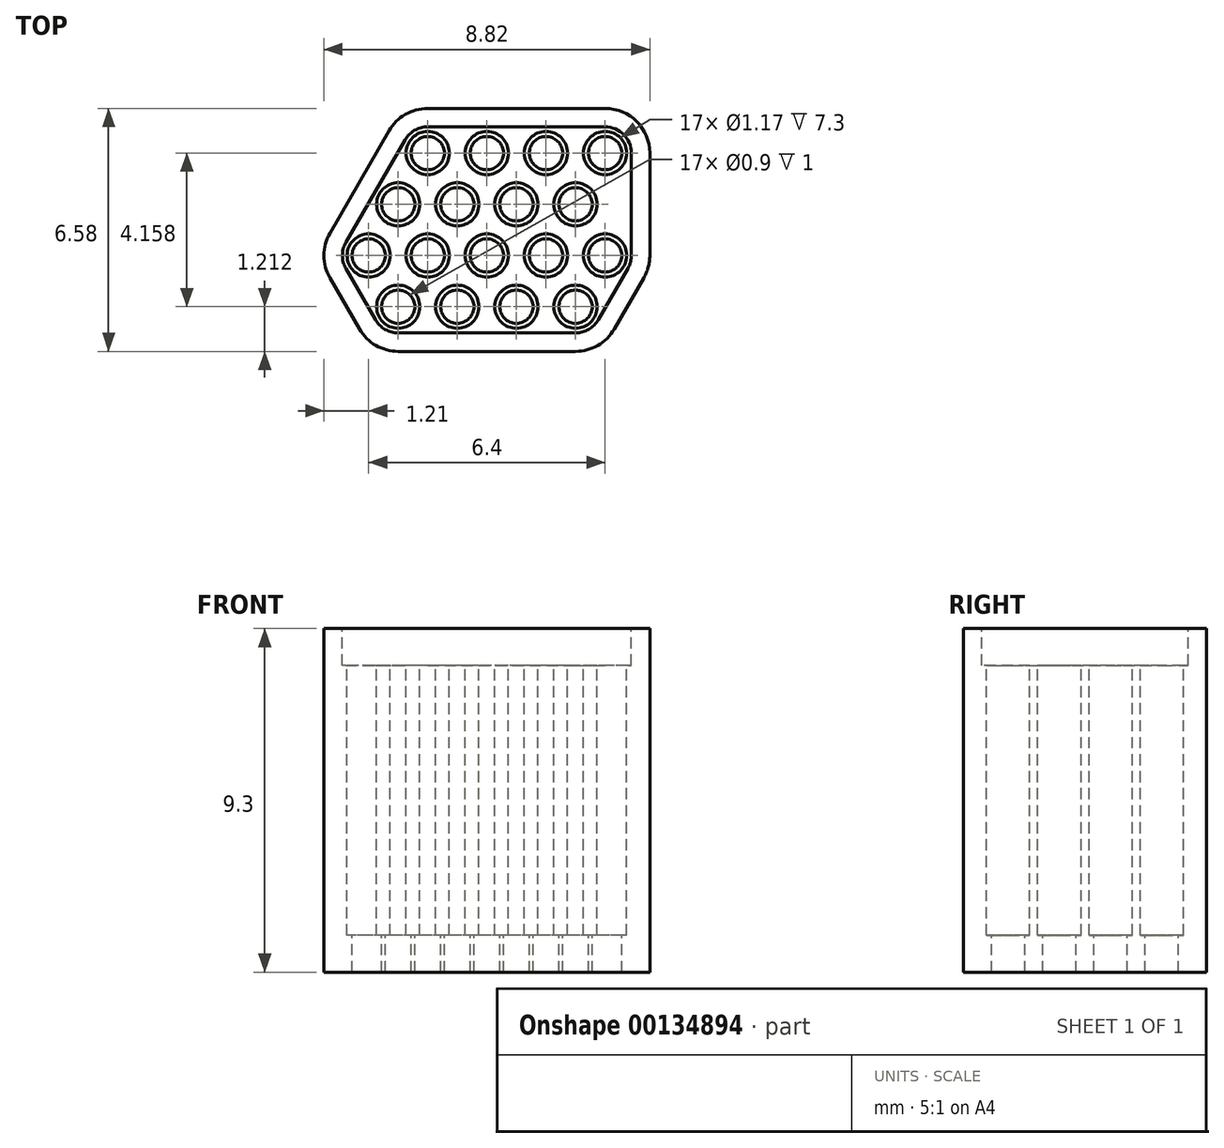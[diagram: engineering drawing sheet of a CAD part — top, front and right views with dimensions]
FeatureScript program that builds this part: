
annotation { "Feature Type Name" : "Feature", "Feature Type Description" : "" }
export const myFeature = defineFeature(function(context is Context, id is Id, definition is map)
    precondition{}
    {
        {
            var Q0;
            Q0=qCreatedBy(makeId("Top.planeOp"),FACE);
            var sketch = newSketch(context, id + "F0", { "sketchPlane" : qUnion([Q0])});
            skLineSegment(sketch, "E0", {"start": v(-0.8, 0) * mm, "end": v(-0.8, -4.16) * mm, "construction": true});
            skCircle(sketch, "E1", {"center": v(0, 0) * mm, "radius": 0.58 * mm});
            skCircle(sketch, "E2", {"center": v(0, -2.77) * mm, "radius": 0.58 * mm});
            skCircle(sketch, "E3", {"center": v(-0.8, -1.39) * mm, "radius": 0.58 * mm});
            skCircle(sketch, "E4", {"center": v(-0.8, -4.16) * mm, "radius": 0.58 * mm});
            skCircle(sketch, "E5.1.0.0", {"center": v(-1.6, 0) * mm, "radius": 0.58 * mm});
            skCircle(sketch, "E5.1.0.1", {"center": v(-2.4, -1.39) * mm, "radius": 0.58 * mm});
            skCircle(sketch, "E5.1.0.2", {"center": v(-2.4, -4.16) * mm, "radius": 0.58 * mm});
            skCircle(sketch, "E5.1.0.3", {"center": v(-1.6, -2.77) * mm, "radius": 0.58 * mm});
            skCircle(sketch, "E5.2.0.0", {"center": v(-3.2, 0) * mm, "radius": 0.58 * mm});
            skCircle(sketch, "E5.2.0.1", {"center": v(-4, -1.39) * mm, "radius": 0.58 * mm});
            skCircle(sketch, "E5.2.0.2", {"center": v(-4, -4.16) * mm, "radius": 0.58 * mm});
            skCircle(sketch, "E5.2.0.3", {"center": v(-3.2, -2.77) * mm, "radius": 0.58 * mm});
            skCircle(sketch, "E5.3.0.0", {"center": v(-4.8, 0) * mm, "radius": 0.58 * mm});
            skCircle(sketch, "E5.3.0.1", {"center": v(-5.6, -1.39) * mm, "radius": 0.58 * mm});
            skCircle(sketch, "E5.3.0.2", {"center": v(-5.6, -4.16) * mm, "radius": 0.58 * mm});
            skCircle(sketch, "E5.3.0.3", {"center": v(-4.8, -2.77) * mm, "radius": 0.58 * mm});
            skLineSegment(sketch, "E5.direction1", {"start": v(-0.8, -4.16) * mm, "end": v(-2.4, -4.16) * mm, "construction": true});
            skCircle(sketch, "E6.1.0.0", {"center": v(-6.4, -2.77) * mm, "radius": 0.58 * mm});
            skLineSegment(sketch, "E6.direction1", {"start": v(-4.8, -2.77) * mm, "end": v(-6.4, -2.77) * mm, "construction": true});
            skLineSegment(sketch, "E7", {"start": v(-6.4, -2.77) * mm, "end": v(-4.8, 0) * mm, "construction": true});
            skLineSegment(sketch, "E8", {"start": v(-4.8, 0) * mm, "end": v(0, 0) * mm, "construction": true});
            skLineSegment(sketch, "E9", {"start": v(0, 0) * mm, "end": v(0, -2.77) * mm, "construction": true});
            skLineSegment(sketch, "E10", {"start": v(0, -2.77) * mm, "end": v(-0.8, -4.16) * mm, "construction": true});
            skLineSegment(sketch, "E11", {"start": v(-5.6, -4.16) * mm, "end": v(-0.8, -4.16) * mm, "construction": true});
            skLineSegment(sketch, "E12", {"start": v(-5.6, -4.16) * mm, "end": v(-6.4, -2.77) * mm, "construction": true});
            skLineSegment(sketch, "E13.0", {"start": v(-6, -4.87) * mm, "end": v(-7.22, -2.77) * mm, "construction": true});
            skLineSegment(sketch, "E13.1", {"start": v(-5.2, 0.7) * mm, "end": v(0.71, 0.71) * mm, "construction": true});
            skLineSegment(sketch, "E13.2", {"start": v(0.71, 0.71) * mm, "end": v(0.71, -2.96) * mm, "construction": true});
            skLineSegment(sketch, "E13.3", {"start": v(-7.22, -2.77) * mm, "end": v(-5.2, 0.71) * mm, "construction": true});
            skLineSegment(sketch, "E13.4", {"start": v(0.71, -2.96) * mm, "end": v(-0.4, -4.87) * mm, "construction": true});
            skLineSegment(sketch, "E13.5", {"start": v(-6, -4.87) * mm, "end": v(-0.4, -4.87) * mm, "construction": true});
            skArc(sketch, "E14", {"start": v(-4.8, 0.7) * mm, "mid": v(-5.16, 0.61) * mm, "end": v(-5.41, 0.35) * mm});
            skArc(sketch, "E15", {"start": v(-7.01, -2.42) * mm, "mid": v(-7.11, -2.77) * mm, "end": v(-7.01, -3.13) * mm});
            skArc(sketch, "E16", {"start": v(-6.21, -4.51) * mm, "mid": v(-5.96, -4.77) * mm, "end": v(-5.6, -4.87) * mm});
            skArc(sketch, "E17", {"start": v(-0.8, -4.87) * mm, "mid": v(-0.44, -4.77) * mm, "end": v(-0.19, -4.51) * mm});
            skArc(sketch, "E18", {"start": v(0.61, -3.13) * mm, "mid": v(0.69, -2.96) * mm, "end": v(0.71, -2.77) * mm});
            skArc(sketch, "E19", {"start": v(0.71, 0) * mm, "mid": v(0.5, 0.5) * mm, "end": v(0, 0.71) * mm});
            skLineSegment(sketch, "E20", {"start": v(-7.01, -2.42) * mm, "end": v(-5.41, 0.35) * mm});
            skLineSegment(sketch, "E21", {"start": v(-4.8, 0.7) * mm, "end": v(0, 0.71) * mm});
            skLineSegment(sketch, "E22", {"start": v(0.71, 0) * mm, "end": v(0.71, -2.77) * mm});
            skLineSegment(sketch, "E23", {"start": v(0.61, -3.13) * mm, "end": v(-0.19, -4.51) * mm});
            skLineSegment(sketch, "E24", {"start": v(-0.8, -4.87) * mm, "end": v(-5.6, -4.87) * mm});
            skLineSegment(sketch, "E25", {"start": v(-6.21, -4.51) * mm, "end": v(-7.01, -3.13) * mm});
            skArc(sketch, "E26.0", {"start": v(-4.8, 1.21) * mm, "mid": v(-5.4, 1.05) * mm, "end": v(-5.85, 0.6) * mm});
            skLineSegment(sketch, "E26.1", {"start": v(1.05, -3.38) * mm, "end": v(0.25, -4.76) * mm});
            skArc(sketch, "E26.2", {"start": v(1.05, -3.38) * mm, "mid": v(1.17, -3.09) * mm, "end": v(1.21, -2.77) * mm});
            skLineSegment(sketch, "E26.3", {"start": v(1.21, 0) * mm, "end": v(1.21, -2.77) * mm});
            skArc(sketch, "E26.4", {"start": v(1.21, 0) * mm, "mid": v(0.86, 0.86) * mm, "end": v(0, 1.21) * mm});
            skArc(sketch, "E26.5", {"start": v(-0.8, -5.37) * mm, "mid": v(-0.2, -5.2) * mm, "end": v(0.25, -4.76) * mm});
            skLineSegment(sketch, "E26.6", {"start": v(-4.8, 1.2) * mm, "end": v(0, 1.21) * mm});
            skLineSegment(sketch, "E26.7", {"start": v(-0.8, -5.37) * mm, "end": v(-5.6, -5.37) * mm});
            skArc(sketch, "E26.8", {"start": v(-6.65, -4.76) * mm, "mid": v(-6.2, -5.2) * mm, "end": v(-5.6, -5.37) * mm});
            skLineSegment(sketch, "E26.9", {"start": v(-6.65, -4.76) * mm, "end": v(-7.45, -3.38) * mm});
            skArc(sketch, "E26.10", {"start": v(-7.45, -2.17) * mm, "mid": v(-7.61, -2.77) * mm, "end": v(-7.45, -3.38) * mm});
            skLineSegment(sketch, "E26.11", {"start": v(-7.45, -2.17) * mm, "end": v(-5.85, 0.6) * mm});
            skSolve(sketch);
        }
        {
            var Q0;
            Q0=makeQuery(id+"F0.imprint","IMPRINT",FACE,{"disambiguationData":[TD([[makeQuery(id+"F0.imprint","IMPRINT",EDGE,{"derivedFrom":sQuery(id+"F0.wireOp",EDGE,"E14")}),-1.0]])]});
            var Q1;
            Q1=makeQuery(id+"F0.imprint","IMPRINT",FACE,{"disambiguationData":[TD([[makeQuery(id+"F0.imprint","IMPRINT",EDGE,{"derivedFrom":sQuery(id+"F0.wireOp",EDGE,"E1")}),-1.0]])]});
            var Q2;
            Q2=makeQuery(id+"F0.imprint","IMPRINT",FACE,{"disambiguationData":[TD([[makeQuery(id+"F0.imprint","IMPRINT",EDGE,{"derivedFrom":sQuery(id+"F0.wireOp",EDGE,"E4")}),1.0]])]});
            var Q3;
            Q3=makeQuery(id+"F0.imprint","IMPRINT",FACE,{"disambiguationData":[TD([[makeQuery(id+"F0.imprint","IMPRINT",EDGE,{"derivedFrom":sQuery(id+"F0.wireOp",EDGE,"E2")}),1.0]])]});
            var Q4;
            Q4=makeQuery(id+"F0.imprint","IMPRINT",FACE,{"disambiguationData":[TD([[makeQuery(id+"F0.imprint","IMPRINT",EDGE,{"derivedFrom":sQuery(id+"F0.wireOp",EDGE,"E3")}),1.0]])]});
            var Q5;
            Q5=makeQuery(id+"F0.imprint","IMPRINT",FACE,{"disambiguationData":[TD([[makeQuery(id+"F0.imprint","IMPRINT",EDGE,{"derivedFrom":sQuery(id+"F0.wireOp",EDGE,"E1")}),1.0]])]});
            var Q6;
            Q6=makeQuery(id+"F0.imprint","IMPRINT",FACE,{"disambiguationData":[TD([[makeQuery(id+"F0.imprint","IMPRINT",EDGE,{"derivedFrom":sQuery(id+"F0.wireOp",EDGE,"E5.1.0.0")}),1.0]])]});
            var Q7;
            Q7=makeQuery(id+"F0.imprint","IMPRINT",FACE,{"disambiguationData":[TD([[makeQuery(id+"F0.imprint","IMPRINT",EDGE,{"derivedFrom":sQuery(id+"F0.wireOp",EDGE,"E5.2.0.0")}),1.0]])]});
            var Q8;
            Q8=makeQuery(id+"F0.imprint","IMPRINT",FACE,{"disambiguationData":[TD([[makeQuery(id+"F0.imprint","IMPRINT",EDGE,{"derivedFrom":sQuery(id+"F0.wireOp",EDGE,"E5.3.0.0")}),1.0]])]});
            var Q9;
            Q9=makeQuery(id+"F0.imprint","IMPRINT",FACE,{"disambiguationData":[TD([[makeQuery(id+"F0.imprint","IMPRINT",EDGE,{"derivedFrom":sQuery(id+"F0.wireOp",EDGE,"E5.3.0.1")}),1.0]])]});
            var Q10;
            Q10=makeQuery(id+"F0.imprint","IMPRINT",FACE,{"disambiguationData":[TD([[makeQuery(id+"F0.imprint","IMPRINT",EDGE,{"derivedFrom":sQuery(id+"F0.wireOp",EDGE,"E5.2.0.1")}),1.0]])]});
            var Q11;
            Q11=makeQuery(id+"F0.imprint","IMPRINT",FACE,{"disambiguationData":[TD([[makeQuery(id+"F0.imprint","IMPRINT",EDGE,{"derivedFrom":sQuery(id+"F0.wireOp",EDGE,"E5.1.0.1")}),1.0]])]});
            var Q12;
            Q12=makeQuery(id+"F0.imprint","IMPRINT",FACE,{"disambiguationData":[TD([[makeQuery(id+"F0.imprint","IMPRINT",EDGE,{"derivedFrom":sQuery(id+"F0.wireOp",EDGE,"E5.1.0.3")}),1.0]])]});
            var Q13;
            Q13=makeQuery(id+"F0.imprint","IMPRINT",FACE,{"disambiguationData":[TD([[makeQuery(id+"F0.imprint","IMPRINT",EDGE,{"derivedFrom":sQuery(id+"F0.wireOp",EDGE,"E5.2.0.3")}),1.0]])]});
            var Q14;
            Q14=makeQuery(id+"F0.imprint","IMPRINT",FACE,{"disambiguationData":[TD([[makeQuery(id+"F0.imprint","IMPRINT",EDGE,{"derivedFrom":sQuery(id+"F0.wireOp",EDGE,"E6.1.0.0")}),1.0]])]});
            var Q15;
            Q15=makeQuery(id+"F0.imprint","IMPRINT",FACE,{"disambiguationData":[TD([[makeQuery(id+"F0.imprint","IMPRINT",EDGE,{"derivedFrom":sQuery(id+"F0.wireOp",EDGE,"E5.3.0.2")}),1.0]])]});
            var Q16;
            Q16=makeQuery(id+"F0.imprint","IMPRINT",FACE,{"disambiguationData":[TD([[makeQuery(id+"F0.imprint","IMPRINT",EDGE,{"derivedFrom":sQuery(id+"F0.wireOp",EDGE,"E5.2.0.2")}),1.0]])]});
            var Q17;
            Q17=makeQuery(id+"F0.imprint","IMPRINT",FACE,{"disambiguationData":[TD([[makeQuery(id+"F0.imprint","IMPRINT",EDGE,{"derivedFrom":sQuery(id+"F0.wireOp",EDGE,"E5.1.0.2")}),1.0]])]});
            var Q18;
            Q18=makeQuery(id+"F0.imprint","IMPRINT",FACE,{"disambiguationData":[TD([[makeQuery(id+"F0.imprint","IMPRINT",EDGE,{"derivedFrom":sQuery(id+"F0.wireOp",EDGE,"E5.3.0.3")}),1.0]])]});
            extrude(context, id + "F1", {"entities" : qUnion([Q0, Q1, Q2, Q3, Q4, Q5, Q6, Q7, Q8, Q9, Q10, Q11, Q12, Q13, Q14, Q15, Q16, Q17, Q18]), "oppositeDirection" : true, "depth" : 9.3 * mm});
        }
        {
            var Q0;
            Q0=makeQuery(id+"F0.imprint","IMPRINT",FACE,{"disambiguationData":[TD([[makeQuery(id+"F0.imprint","IMPRINT",EDGE,{"derivedFrom":sQuery(id+"F0.wireOp",EDGE,"E1")}),-1.0]])]});
            var Q1;
            Q1=makeQuery(id+"F0.imprint","IMPRINT",FACE,{"disambiguationData":[TD([[makeQuery(id+"F0.imprint","IMPRINT",EDGE,{"derivedFrom":sQuery(id+"F0.wireOp",EDGE,"E5.3.0.0")}),1.0]])]});
            var Q2;
            Q2=makeQuery(id+"F0.imprint","IMPRINT",FACE,{"disambiguationData":[TD([[makeQuery(id+"F0.imprint","IMPRINT",EDGE,{"derivedFrom":sQuery(id+"F0.wireOp",EDGE,"E5.3.0.1")}),1.0]])]});
            var Q3;
            Q3=makeQuery(id+"F0.imprint","IMPRINT",FACE,{"disambiguationData":[TD([[makeQuery(id+"F0.imprint","IMPRINT",EDGE,{"derivedFrom":sQuery(id+"F0.wireOp",EDGE,"E6.1.0.0")}),1.0]])]});
            var Q4;
            Q4=makeQuery(id+"F0.imprint","IMPRINT",FACE,{"disambiguationData":[TD([[makeQuery(id+"F0.imprint","IMPRINT",EDGE,{"derivedFrom":sQuery(id+"F0.wireOp",EDGE,"E5.3.0.2")}),1.0]])]});
            var Q5;
            Q5=makeQuery(id+"F0.imprint","IMPRINT",FACE,{"disambiguationData":[TD([[makeQuery(id+"F0.imprint","IMPRINT",EDGE,{"derivedFrom":sQuery(id+"F0.wireOp",EDGE,"E5.3.0.3")}),1.0]])]});
            var Q6;
            Q6=makeQuery(id+"F0.imprint","IMPRINT",FACE,{"disambiguationData":[TD([[makeQuery(id+"F0.imprint","IMPRINT",EDGE,{"derivedFrom":sQuery(id+"F0.wireOp",EDGE,"E5.2.0.2")}),1.0]])]});
            var Q7;
            Q7=makeQuery(id+"F0.imprint","IMPRINT",FACE,{"disambiguationData":[TD([[makeQuery(id+"F0.imprint","IMPRINT",EDGE,{"derivedFrom":sQuery(id+"F0.wireOp",EDGE,"E5.2.0.1")}),1.0]])]});
            var Q8;
            Q8=makeQuery(id+"F0.imprint","IMPRINT",FACE,{"disambiguationData":[TD([[makeQuery(id+"F0.imprint","IMPRINT",EDGE,{"derivedFrom":sQuery(id+"F0.wireOp",EDGE,"E5.2.0.0")}),1.0]])]});
            var Q9;
            Q9=makeQuery(id+"F0.imprint","IMPRINT",FACE,{"disambiguationData":[TD([[makeQuery(id+"F0.imprint","IMPRINT",EDGE,{"derivedFrom":sQuery(id+"F0.wireOp",EDGE,"E5.1.0.0")}),1.0]])]});
            var Q10;
            Q10=makeQuery(id+"F0.imprint","IMPRINT",FACE,{"disambiguationData":[TD([[makeQuery(id+"F0.imprint","IMPRINT",EDGE,{"derivedFrom":sQuery(id+"F0.wireOp",EDGE,"E5.1.0.1")}),1.0]])]});
            var Q11;
            Q11=makeQuery(id+"F0.imprint","IMPRINT",FACE,{"disambiguationData":[TD([[makeQuery(id+"F0.imprint","IMPRINT",EDGE,{"derivedFrom":sQuery(id+"F0.wireOp",EDGE,"E5.2.0.3")}),1.0]])]});
            var Q12;
            Q12=makeQuery(id+"F0.imprint","IMPRINT",FACE,{"disambiguationData":[TD([[makeQuery(id+"F0.imprint","IMPRINT",EDGE,{"derivedFrom":sQuery(id+"F0.wireOp",EDGE,"E5.1.0.2")}),1.0]])]});
            var Q13;
            Q13=makeQuery(id+"F0.imprint","IMPRINT",FACE,{"disambiguationData":[TD([[makeQuery(id+"F0.imprint","IMPRINT",EDGE,{"derivedFrom":sQuery(id+"F0.wireOp",EDGE,"E1")}),1.0]])]});
            var Q14;
            Q14=makeQuery(id+"F0.imprint","IMPRINT",FACE,{"disambiguationData":[TD([[makeQuery(id+"F0.imprint","IMPRINT",EDGE,{"derivedFrom":sQuery(id+"F0.wireOp",EDGE,"E3")}),1.0]])]});
            var Q15;
            Q15=makeQuery(id+"F0.imprint","IMPRINT",FACE,{"disambiguationData":[TD([[makeQuery(id+"F0.imprint","IMPRINT",EDGE,{"derivedFrom":sQuery(id+"F0.wireOp",EDGE,"E5.1.0.3")}),1.0]])]});
            var Q16;
            Q16=makeQuery(id+"F0.imprint","IMPRINT",FACE,{"disambiguationData":[TD([[makeQuery(id+"F0.imprint","IMPRINT",EDGE,{"derivedFrom":sQuery(id+"F0.wireOp",EDGE,"E4")}),1.0]])]});
            var Q17;
            Q17=makeQuery(id+"F0.imprint","IMPRINT",FACE,{"disambiguationData":[TD([[makeQuery(id+"F0.imprint","IMPRINT",EDGE,{"derivedFrom":sQuery(id+"F0.wireOp",EDGE,"E2")}),1.0]])]});
            extrude(context, id + "F2", {"entities" : qUnion([Q0, Q1, Q2, Q3, Q4, Q5, Q6, Q7, Q8, Q9, Q10, Q11, Q12, Q13, Q14, Q15, Q16, Q17]), "operationType" : NewBodyOperationType.REMOVE, "oppositeDirection" : true, "depth" : 1 * mm});
        }
        {
            var Q0;
            Q0=makeQuery(id+"F0.imprint","IMPRINT",FACE,{"disambiguationData":[TD([[makeQuery(id+"F0.imprint","IMPRINT",EDGE,{"derivedFrom":sQuery(id+"F0.wireOp",EDGE,"E6.1.0.0")}),1.0]])]});
            var Q1;
            Q1=makeQuery(id+"F0.imprint","IMPRINT",FACE,{"disambiguationData":[TD([[makeQuery(id+"F0.imprint","IMPRINT",EDGE,{"derivedFrom":sQuery(id+"F0.wireOp",EDGE,"E5.3.0.1")}),1.0]])]});
            var Q2;
            Q2=makeQuery(id+"F0.imprint","IMPRINT",FACE,{"disambiguationData":[TD([[makeQuery(id+"F0.imprint","IMPRINT",EDGE,{"derivedFrom":sQuery(id+"F0.wireOp",EDGE,"E5.3.0.0")}),1.0]])]});
            var Q3;
            Q3=makeQuery(id+"F0.imprint","IMPRINT",FACE,{"disambiguationData":[TD([[makeQuery(id+"F0.imprint","IMPRINT",EDGE,{"derivedFrom":sQuery(id+"F0.wireOp",EDGE,"E5.3.0.2")}),1.0]])]});
            var Q4;
            Q4=makeQuery(id+"F0.imprint","IMPRINT",FACE,{"disambiguationData":[TD([[makeQuery(id+"F0.imprint","IMPRINT",EDGE,{"derivedFrom":sQuery(id+"F0.wireOp",EDGE,"E5.3.0.3")}),1.0]])]});
            var Q5;
            Q5=makeQuery(id+"F0.imprint","IMPRINT",FACE,{"disambiguationData":[TD([[makeQuery(id+"F0.imprint","IMPRINT",EDGE,{"derivedFrom":sQuery(id+"F0.wireOp",EDGE,"E5.2.0.1")}),1.0]])]});
            var Q6;
            Q6=makeQuery(id+"F0.imprint","IMPRINT",FACE,{"disambiguationData":[TD([[makeQuery(id+"F0.imprint","IMPRINT",EDGE,{"derivedFrom":sQuery(id+"F0.wireOp",EDGE,"E5.2.0.0")}),1.0]])]});
            var Q7;
            Q7=makeQuery(id+"F0.imprint","IMPRINT",FACE,{"disambiguationData":[TD([[makeQuery(id+"F0.imprint","IMPRINT",EDGE,{"derivedFrom":sQuery(id+"F0.wireOp",EDGE,"E5.1.0.0")}),1.0]])]});
            var Q8;
            Q8=makeQuery(id+"F0.imprint","IMPRINT",FACE,{"disambiguationData":[TD([[makeQuery(id+"F0.imprint","IMPRINT",EDGE,{"derivedFrom":sQuery(id+"F0.wireOp",EDGE,"E5.1.0.1")}),1.0]])]});
            var Q9;
            Q9=makeQuery(id+"F0.imprint","IMPRINT",FACE,{"disambiguationData":[TD([[makeQuery(id+"F0.imprint","IMPRINT",EDGE,{"derivedFrom":sQuery(id+"F0.wireOp",EDGE,"E5.2.0.3")}),1.0]])]});
            var Q10;
            Q10=makeQuery(id+"F0.imprint","IMPRINT",FACE,{"disambiguationData":[TD([[makeQuery(id+"F0.imprint","IMPRINT",EDGE,{"derivedFrom":sQuery(id+"F0.wireOp",EDGE,"E5.2.0.2")}),1.0]])]});
            var Q11;
            Q11=makeQuery(id+"F0.imprint","IMPRINT",FACE,{"disambiguationData":[TD([[makeQuery(id+"F0.imprint","IMPRINT",EDGE,{"derivedFrom":sQuery(id+"F0.wireOp",EDGE,"E5.1.0.2")}),1.0]])]});
            var Q12;
            Q12=makeQuery(id+"F0.imprint","IMPRINT",FACE,{"disambiguationData":[TD([[makeQuery(id+"F0.imprint","IMPRINT",EDGE,{"derivedFrom":sQuery(id+"F0.wireOp",EDGE,"E5.1.0.3")}),1.0]])]});
            var Q13;
            Q13=makeQuery(id+"F0.imprint","IMPRINT",FACE,{"disambiguationData":[TD([[makeQuery(id+"F0.imprint","IMPRINT",EDGE,{"derivedFrom":sQuery(id+"F0.wireOp",EDGE,"E3")}),1.0]])]});
            var Q14;
            Q14=makeQuery(id+"F0.imprint","IMPRINT",FACE,{"disambiguationData":[TD([[makeQuery(id+"F0.imprint","IMPRINT",EDGE,{"derivedFrom":sQuery(id+"F0.wireOp",EDGE,"E1")}),1.0]])]});
            var Q15;
            Q15=makeQuery(id+"F0.imprint","IMPRINT",FACE,{"disambiguationData":[TD([[makeQuery(id+"F0.imprint","IMPRINT",EDGE,{"derivedFrom":sQuery(id+"F0.wireOp",EDGE,"E2")}),1.0]])]});
            var Q16;
            Q16=makeQuery(id+"F0.imprint","IMPRINT",FACE,{"disambiguationData":[TD([[makeQuery(id+"F0.imprint","IMPRINT",EDGE,{"derivedFrom":sQuery(id+"F0.wireOp",EDGE,"E4")}),1.0]])]});
            var Q17;
            Q17=makeQuery(id+"F0.imprint","IMPRINT",FACE,{"disambiguationData":[TD([[makeQuery(id+"F0.imprint","IMPRINT",EDGE,{"derivedFrom":sQuery(id+"F0.wireOp",EDGE,"E4")}),1.0]])]});
            var Q18;
            Q18=makeQuery(id+"F0.imprint","IMPRINT",FACE,{"disambiguationData":[TD([[makeQuery(id+"F0.imprint","IMPRINT",EDGE,{"derivedFrom":sQuery(id+"F0.wireOp",EDGE,"E5.2.0.2")}),1.0]])]});
            var Q19;
            Q19=makeQuery(id+"F0.imprint","IMPRINT",FACE,{"disambiguationData":[TD([[makeQuery(id+"F0.imprint","IMPRINT",EDGE,{"derivedFrom":sQuery(id+"F0.wireOp",EDGE,"E5.1.0.2")}),1.0]])]});
            var Q20;
            Q20=makeQuery(id+"F0.imprint","IMPRINT",FACE,{"disambiguationData":[TD([[makeQuery(id+"F0.imprint","IMPRINT",EDGE,{"derivedFrom":sQuery(id+"F0.wireOp",EDGE,"E5.1.0.3")}),1.0]])]});
            var Q21;
            Q21=makeQuery(id+"F0.imprint","IMPRINT",FACE,{"disambiguationData":[TD([[makeQuery(id+"F0.imprint","IMPRINT",EDGE,{"derivedFrom":sQuery(id+"F0.wireOp",EDGE,"E3")}),1.0]])]});
            var Q22;
            Q22=makeQuery(id+"F0.imprint","IMPRINT",FACE,{"disambiguationData":[TD([[makeQuery(id+"F0.imprint","IMPRINT",EDGE,{"derivedFrom":sQuery(id+"F0.wireOp",EDGE,"E1")}),1.0]])]});
            var Q23;
            Q23=makeQuery(id+"F0.imprint","IMPRINT",FACE,{"disambiguationData":[TD([[makeQuery(id+"F0.imprint","IMPRINT",EDGE,{"derivedFrom":sQuery(id+"F0.wireOp",EDGE,"E2")}),1.0]])]});
            var Q24;
            Q24=makeQuery(id+"F0.imprint","IMPRINT",FACE,{"disambiguationData":[TD([[makeQuery(id+"F0.imprint","IMPRINT",EDGE,{"derivedFrom":sQuery(id+"F0.wireOp",EDGE,"E4")}),1.0]])]});
            extrude(context, id + "F3", {"entities" : qUnion([Q0, Q1, Q2, Q3, Q4, Q5, Q6, Q7, Q8, Q9, Q10, Q11, Q12, Q13, Q14, Q15, Q16, Q17, Q18, Q19, Q20, Q21, Q22, Q23, Q24]), "operationType" : NewBodyOperationType.REMOVE, "oppositeDirection" : true, "depth" : 8.3 * mm});
        }
        {
            var Q0;
            Q0=qCreatedBy(makeId("Top.planeOp"),FACE);
            var sketch = newSketch(context, id + "F4", { "sketchPlane" : qUnion([Q0])});
            skLineSegment(sketch, "E27", {"start": v(-0.8, 0) * mm, "end": v(-0.8, -4.16) * mm, "construction": true});
            skCircle(sketch, "E28", {"center": v(0, 0) * mm, "radius": 0.58 * mm, "construction": true});
            skCircle(sketch, "E29", {"center": v(0, -2.77) * mm, "radius": 0.58 * mm, "construction": true});
            skCircle(sketch, "E30", {"center": v(-0.8, -1.39) * mm, "radius": 0.58 * mm, "construction": true});
            skCircle(sketch, "E31", {"center": v(-0.8, -4.16) * mm, "radius": 0.58 * mm, "construction": true});
            skCircle(sketch, "E32.1.0.0", {"center": v(-1.6, 0) * mm, "radius": 0.58 * mm, "construction": true});
            skCircle(sketch, "E32.1.0.1", {"center": v(-2.4, -1.39) * mm, "radius": 0.58 * mm, "construction": true});
            skCircle(sketch, "E32.1.0.2", {"center": v(-2.4, -4.16) * mm, "radius": 0.58 * mm, "construction": true});
            skCircle(sketch, "E32.1.0.3", {"center": v(-1.6, -2.77) * mm, "radius": 0.58 * mm, "construction": true});
            skCircle(sketch, "E32.2.0.0", {"center": v(-3.2, 0) * mm, "radius": 0.58 * mm, "construction": true});
            skCircle(sketch, "E32.2.0.1", {"center": v(-4, -1.39) * mm, "radius": 0.58 * mm, "construction": true});
            skCircle(sketch, "E32.2.0.2", {"center": v(-4, -4.16) * mm, "radius": 0.58 * mm, "construction": true});
            skCircle(sketch, "E32.2.0.3", {"center": v(-3.2, -2.77) * mm, "radius": 0.58 * mm, "construction": true});
            skCircle(sketch, "E32.3.0.0", {"center": v(-4.8, 0) * mm, "radius": 0.58 * mm, "construction": true});
            skCircle(sketch, "E32.3.0.1", {"center": v(-5.6, -1.39) * mm, "radius": 0.58 * mm, "construction": true});
            skCircle(sketch, "E32.3.0.2", {"center": v(-5.6, -4.16) * mm, "radius": 0.58 * mm, "construction": true});
            skCircle(sketch, "E32.3.0.3", {"center": v(-4.8, -2.77) * mm, "radius": 0.58 * mm, "construction": true});
            skLineSegment(sketch, "E32.direction1", {"start": v(-0.8, -4.16) * mm, "end": v(-2.4, -4.16) * mm, "construction": true});
            skCircle(sketch, "E33.1.0.0", {"center": v(-6.4, -2.77) * mm, "radius": 0.58 * mm, "construction": true});
            skLineSegment(sketch, "E33.direction1", {"start": v(-4.8, -2.77) * mm, "end": v(-6.4, -2.77) * mm, "construction": true});
            skCircle(sketch, "E34", {"center": v(0, 0) * mm, "radius": 0.45 * mm});
            skCircle(sketch, "E35", {"center": v(-0.8, -1.39) * mm, "radius": 0.45 * mm});
            skCircle(sketch, "E36", {"center": v(0, -2.77) * mm, "radius": 0.45 * mm});
            skCircle(sketch, "E37", {"center": v(-0.8, -4.16) * mm, "radius": 0.45 * mm});
            skCircle(sketch, "E38.1.0.0", {"center": v(-1.6, 0) * mm, "radius": 0.45 * mm});
            skCircle(sketch, "E38.1.0.1", {"center": v(-2.4, -1.39) * mm, "radius": 0.45 * mm});
            skCircle(sketch, "E38.1.0.2", {"center": v(-1.6, -2.77) * mm, "radius": 0.45 * mm});
            skCircle(sketch, "E38.1.0.3", {"center": v(-2.4, -4.16) * mm, "radius": 0.45 * mm});
            skCircle(sketch, "E38.2.0.0", {"center": v(-3.2, 0) * mm, "radius": 0.45 * mm});
            skCircle(sketch, "E38.2.0.1", {"center": v(-4, -1.39) * mm, "radius": 0.45 * mm});
            skCircle(sketch, "E38.2.0.2", {"center": v(-3.2, -2.77) * mm, "radius": 0.45 * mm});
            skCircle(sketch, "E38.2.0.3", {"center": v(-4, -4.16) * mm, "radius": 0.45 * mm});
            skCircle(sketch, "E38.3.0.0", {"center": v(-4.8, 0) * mm, "radius": 0.45 * mm});
            skCircle(sketch, "E38.3.0.1", {"center": v(-5.6, -1.39) * mm, "radius": 0.45 * mm});
            skCircle(sketch, "E38.3.0.2", {"center": v(-4.8, -2.77) * mm, "radius": 0.45 * mm});
            skCircle(sketch, "E38.3.0.3", {"center": v(-5.6, -4.16) * mm, "radius": 0.45 * mm});
            skCircle(sketch, "E39.1.0.0", {"center": v(-6.4, -2.77) * mm, "radius": 0.45 * mm});
            skSolve(sketch);
        }
        {
            var Q0;
            Q0=makeQuery(id+"F4.imprint","IMPRINT",FACE,{"disambiguationData":[TD([[makeQuery(id+"F4.imprint","IMPRINT",EDGE,{"derivedFrom":sQuery(id+"F4.wireOp",EDGE,"E38.3.0.0")}),1.0]])]});
            var Q1;
            Q1=makeQuery(id+"F4.imprint","IMPRINT",FACE,{"disambiguationData":[TD([[makeQuery(id+"F4.imprint","IMPRINT",EDGE,{"derivedFrom":sQuery(id+"F4.wireOp",EDGE,"E38.2.0.0")}),1.0]])]});
            var Q2;
            Q2=makeQuery(id+"F4.imprint","IMPRINT",FACE,{"disambiguationData":[TD([[makeQuery(id+"F4.imprint","IMPRINT",EDGE,{"derivedFrom":sQuery(id+"F4.wireOp",EDGE,"E38.1.0.0")}),1.0]])]});
            var Q3;
            Q3=makeQuery(id+"F4.imprint","IMPRINT",FACE,{"disambiguationData":[TD([[makeQuery(id+"F4.imprint","IMPRINT",EDGE,{"derivedFrom":sQuery(id+"F4.wireOp",EDGE,"E34")}),1.0]])]});
            var Q4;
            Q4=makeQuery(id+"F4.imprint","IMPRINT",FACE,{"disambiguationData":[TD([[makeQuery(id+"F4.imprint","IMPRINT",EDGE,{"derivedFrom":sQuery(id+"F4.wireOp",EDGE,"E35")}),1.0]])]});
            var Q5;
            Q5=makeQuery(id+"F4.imprint","IMPRINT",FACE,{"disambiguationData":[TD([[makeQuery(id+"F4.imprint","IMPRINT",EDGE,{"derivedFrom":sQuery(id+"F4.wireOp",EDGE,"E38.1.0.1")}),1.0]])]});
            var Q6;
            Q6=makeQuery(id+"F4.imprint","IMPRINT",FACE,{"disambiguationData":[TD([[makeQuery(id+"F4.imprint","IMPRINT",EDGE,{"derivedFrom":sQuery(id+"F4.wireOp",EDGE,"E38.2.0.1")}),1.0]])]});
            var Q7;
            Q7=makeQuery(id+"F4.imprint","IMPRINT",FACE,{"disambiguationData":[TD([[makeQuery(id+"F4.imprint","IMPRINT",EDGE,{"derivedFrom":sQuery(id+"F4.wireOp",EDGE,"E38.3.0.1")}),1.0]])]});
            var Q8;
            Q8=makeQuery(id+"F4.imprint","IMPRINT",FACE,{"disambiguationData":[TD([[makeQuery(id+"F4.imprint","IMPRINT",EDGE,{"derivedFrom":sQuery(id+"F4.wireOp",EDGE,"E39.1.0.0")}),1.0]])]});
            var Q9;
            Q9=makeQuery(id+"F4.imprint","IMPRINT",FACE,{"disambiguationData":[TD([[makeQuery(id+"F4.imprint","IMPRINT",EDGE,{"derivedFrom":sQuery(id+"F4.wireOp",EDGE,"E38.3.0.2")}),1.0]])]});
            var Q10;
            Q10=makeQuery(id+"F4.imprint","IMPRINT",FACE,{"disambiguationData":[TD([[makeQuery(id+"F4.imprint","IMPRINT",EDGE,{"derivedFrom":sQuery(id+"F4.wireOp",EDGE,"E38.2.0.2")}),1.0]])]});
            var Q11;
            Q11=makeQuery(id+"F4.imprint","IMPRINT",FACE,{"disambiguationData":[TD([[makeQuery(id+"F4.imprint","IMPRINT",EDGE,{"derivedFrom":sQuery(id+"F4.wireOp",EDGE,"E38.1.0.2")}),1.0]])]});
            var Q12;
            Q12=makeQuery(id+"F4.imprint","IMPRINT",FACE,{"disambiguationData":[TD([[makeQuery(id+"F4.imprint","IMPRINT",EDGE,{"derivedFrom":sQuery(id+"F4.wireOp",EDGE,"E36")}),1.0]])]});
            var Q13;
            Q13=makeQuery(id+"F4.imprint","IMPRINT",FACE,{"disambiguationData":[TD([[makeQuery(id+"F4.imprint","IMPRINT",EDGE,{"derivedFrom":sQuery(id+"F4.wireOp",EDGE,"E37")}),1.0]])]});
            var Q14;
            Q14=makeQuery(id+"F4.imprint","IMPRINT",FACE,{"disambiguationData":[TD([[makeQuery(id+"F4.imprint","IMPRINT",EDGE,{"derivedFrom":sQuery(id+"F4.wireOp",EDGE,"E38.1.0.3")}),1.0]])]});
            var Q15;
            Q15=makeQuery(id+"F4.imprint","IMPRINT",FACE,{"disambiguationData":[TD([[makeQuery(id+"F4.imprint","IMPRINT",EDGE,{"derivedFrom":sQuery(id+"F4.wireOp",EDGE,"E38.2.0.3")}),1.0]])]});
            var Q16;
            Q16=makeQuery(id+"F4.imprint","IMPRINT",FACE,{"disambiguationData":[TD([[makeQuery(id+"F4.imprint","IMPRINT",EDGE,{"derivedFrom":sQuery(id+"F4.wireOp",EDGE,"E38.3.0.3")}),1.0]])]});
            extrude(context, id + "F5", {"entities" : qUnion([Q0, Q1, Q2, Q3, Q4, Q5, Q6, Q7, Q8, Q9, Q10, Q11, Q12, Q13, Q14, Q15, Q16]), "operationType" : NewBodyOperationType.REMOVE, "endBound" : BoundingType.THROUGH_ALL, "oppositeDirection" : true, "depth" : 25 * mm});
        }
    });
